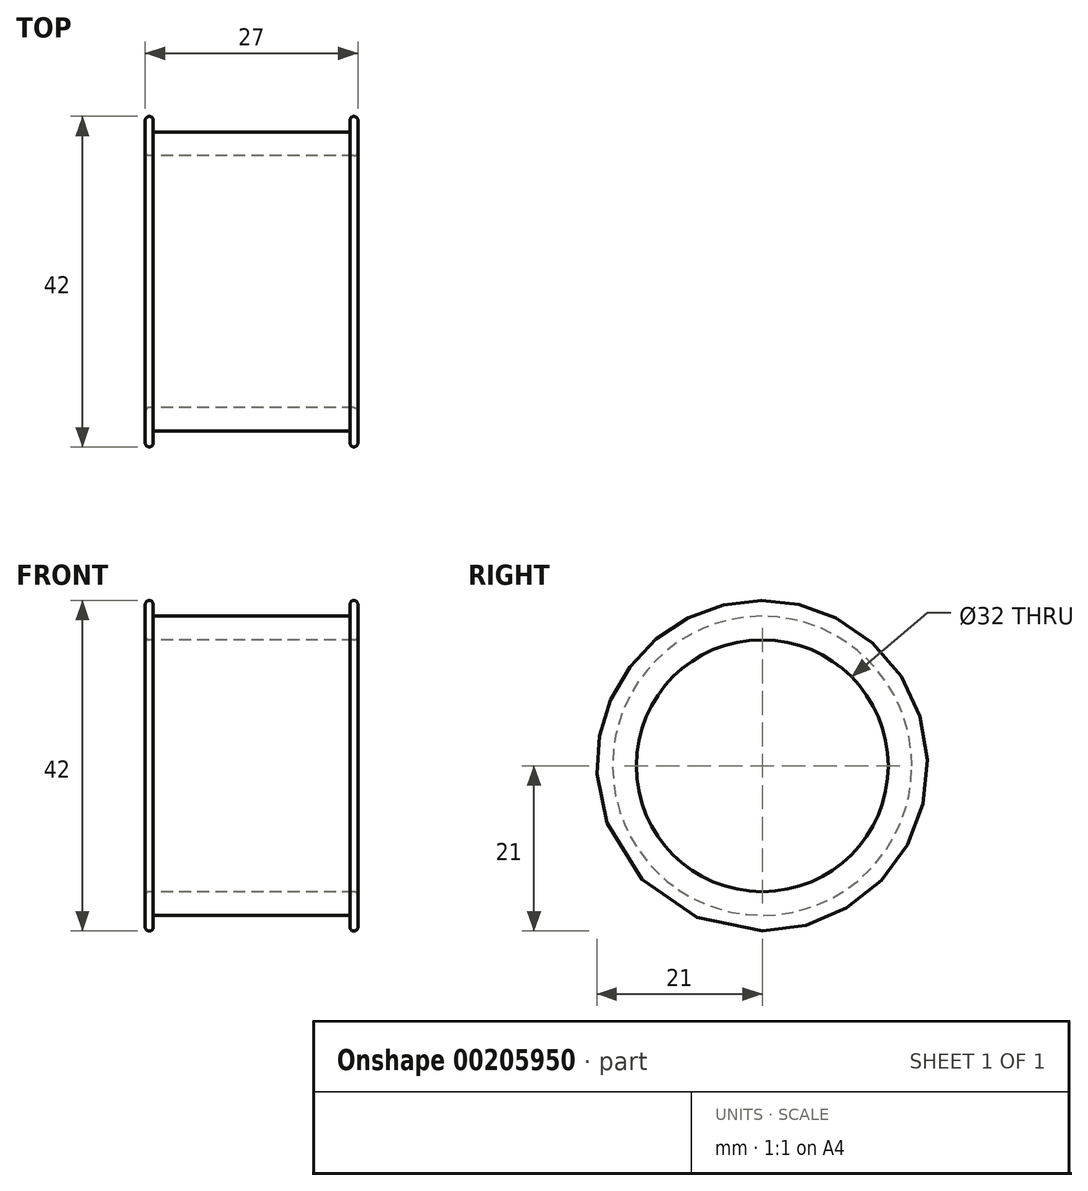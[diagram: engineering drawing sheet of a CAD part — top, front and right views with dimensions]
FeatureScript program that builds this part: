
annotation { "Feature Type Name" : "Feature", "Feature Type Description" : "" }
export const myFeature = defineFeature(function(context is Context, id is Id, definition is map)
    precondition{}
    {
        {
            var Q0;
            Q0=qCreatedBy(makeId("Front.planeOp"),FACE);
            var sketch = newSketch(context, id + "F0", { "sketchPlane" : qUnion([Q0])});
            skLineSegment(sketch, "E0.1", {"start": v(-19.46, 19) * mm, "end": v(5.54, 19) * mm, "construction": true});
            skLineSegment(sketch, "E1.0", {"start": v(-20.46, 16) * mm, "end": v(6.54, 16) * mm, "construction": true});
            skLineSegment(sketch, "E2", {"start": v(-20.46, 16) * mm, "end": v(-20.46, 21) * mm});
            skLineSegment(sketch, "E3", {"start": v(-20.46, 21) * mm, "end": v(-19.46, 21) * mm});
            skLineSegment(sketch, "E4", {"start": v(-19.46, 21) * mm, "end": v(-19.46, 19) * mm});
            skLineSegment(sketch, "E5", {"start": v(5.54, 19) * mm, "end": v(5.54, 21) * mm});
            skLineSegment(sketch, "E6", {"start": v(5.54, 21) * mm, "end": v(6.54, 21) * mm});
            skLineSegment(sketch, "E7", {"start": v(6.54, 16) * mm, "end": v(-20.46, 16) * mm});
            skLineSegment(sketch, "E8", {"start": v(-19.46, 19) * mm, "end": v(5.54, 19) * mm});
            skLineSegment(sketch, "E9", {"start": v(6.54, 21) * mm, "end": v(6.54, 16) * mm});
            skSolve(sketch);
        }
        {
            var Q0;
            Q0=qCreatedBy(makeId("Front.planeOp"),FACE);
            var sketch = newSketch(context, id + "F1", { "sketchPlane" : qUnion([Q0])});
            skLineSegment(sketch, "E10", {"start": v(-29.78, 0) * mm, "end": v(17.76, 0) * mm, "construction": true});
            skSolve(sketch);
        }
        {
            var Q0;
            Q0=makeQuery(id+"F0.imprint","IMPRINT",FACE,{"disambiguationData":[TD([[makeQuery(id+"F0.imprint","IMPRINT",EDGE,{"derivedFrom":sQuery(id+"F0.wireOp",EDGE,"E2")}),-1.0]])]});
            var Q1;
            Q1=sQuery(id+"F1.wireOp",EDGE,"E10");
            revolve(context, id + "F2", {"entities" : qUnion([Q0]), "axis" : qUnion([Q1]), "revolveType" : RevolveType.FULL});
        }
        {
            var Q0;
            Q0=makeQuery(id+"F2.opRevolve","SWEPT_EDGE",EDGE,{"disambiguationData":[OSD([sQuery(id+"F0.wireOp",EDGE,"E6"),sQuery(id+"F0.wireOp",EDGE,"E9")])]});
            var Q1;
            Q1=makeQuery(id+"F2.opRevolve","SWEPT_EDGE",EDGE,{"disambiguationData":[OSD([sQuery(id+"F0.wireOp",EDGE,"E5"),sQuery(id+"F0.wireOp",EDGE,"E6")])]});
            var Q2;
            Q2=makeQuery(id+"F2.opRevolve","SWEPT_EDGE",EDGE,{"disambiguationData":[OSD([sQuery(id+"F0.wireOp",EDGE,"E3"),sQuery(id+"F0.wireOp",EDGE,"E4")])]});
            var Q3;
            Q3=makeQuery(id+"F2.opRevolve","SWEPT_EDGE",EDGE,{"disambiguationData":[OSD([sQuery(id+"F0.wireOp",EDGE,"E2"),sQuery(id+"F0.wireOp",EDGE,"E3")])]});
            fillet(context, id + "F3", {"entities" : qUnion([Q0, Q1, Q2, Q3]), "radius" : 0.5 * mm, "tangentPropagation" : true, "allowEdgeOverflow" : false});
        }
        {
            var Q0;
            Q0=makeQuery(id+"F2.opRevolve","SWEPT_EDGE",EDGE,{"disambiguationData":[OSD([sQuery(id+"F0.wireOp",EDGE,"E2"),sQuery(id+"F0.wireOp",EDGE,"E7")])]});
            var Q1;
            Q1=makeQuery(id+"F2.opRevolve","SWEPT_EDGE",EDGE,{"disambiguationData":[OSD([sQuery(id+"F0.wireOp",EDGE,"E7"),sQuery(id+"F0.wireOp",EDGE,"E9")])]});
            fillet(context, id + "F4", {"entities" : qUnion([Q0, Q1]), "radius" : 0.5 * mm, "tangentPropagation" : true, "allowEdgeOverflow" : false});
        }
    });
